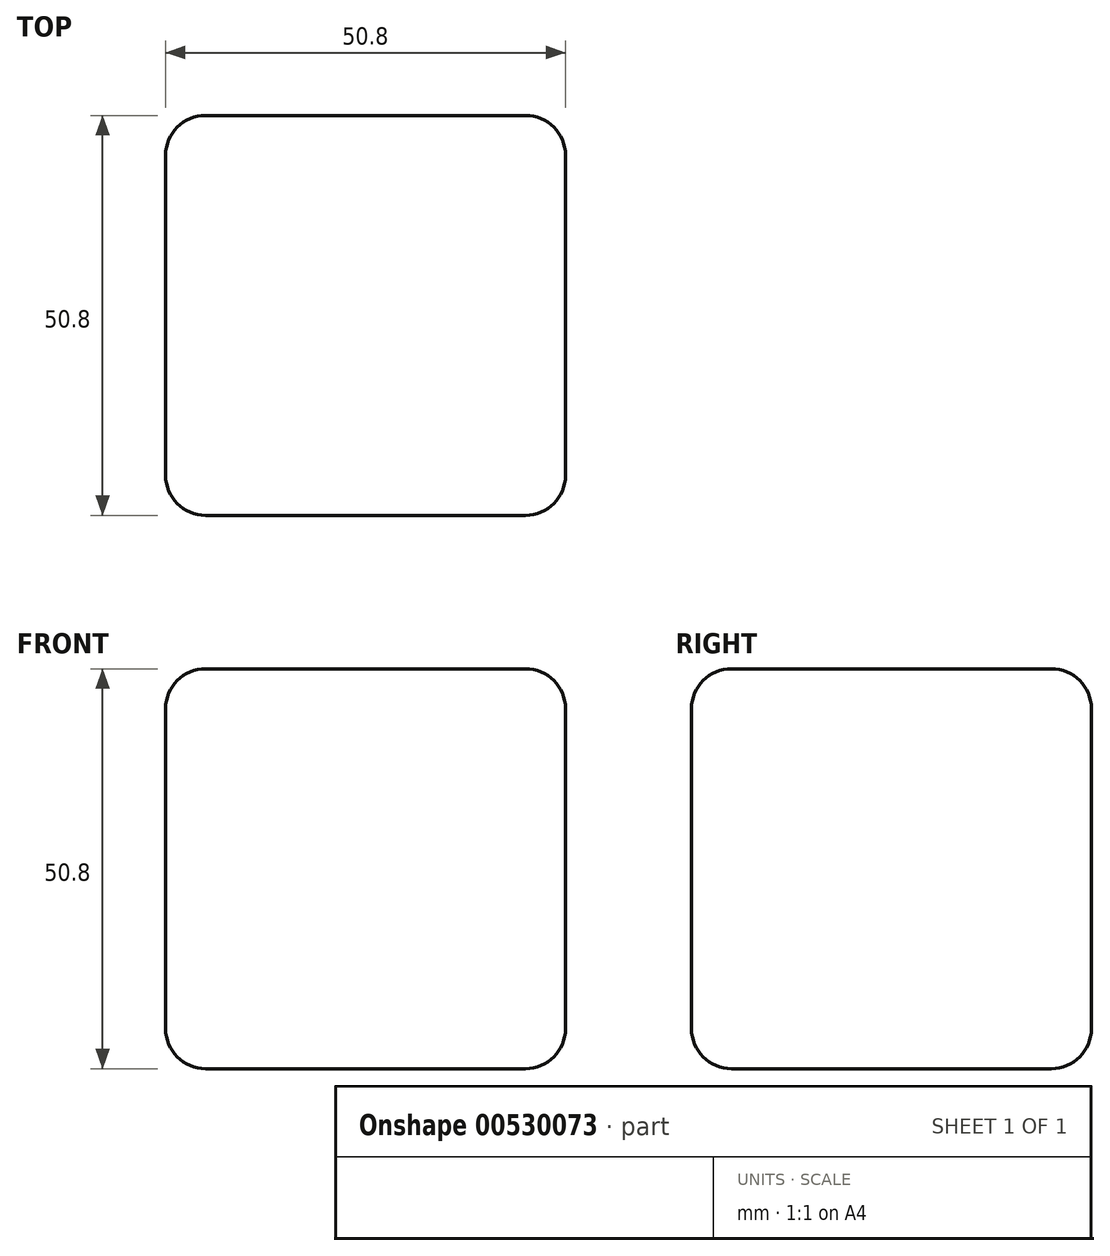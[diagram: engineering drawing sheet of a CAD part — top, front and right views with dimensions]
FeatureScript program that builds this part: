
annotation { "Feature Type Name" : "Feature", "Feature Type Description" : "" }
export const myFeature = defineFeature(function(context is Context, id is Id, definition is map)
    precondition{}
    {
        {
            var Q0;
            Q0=qCreatedBy(makeId("Front.planeOp"),FACE);
            var sketch = newSketch(context, id + "F0", { "sketchPlane" : qUnion([Q0])});
            skLineSegment(sketch, "E0.bottom", {"start": v(0, 0) * mm, "end": v(50.8, 0) * mm});
            skLineSegment(sketch, "E0.top", {"start": v(0, 50.8) * mm, "end": v(50.8, 50.8) * mm});
            skLineSegment(sketch, "E0.left", {"start": v(0, 0) * mm, "end": v(0, 50.8) * mm});
            skLineSegment(sketch, "E0.right", {"start": v(50.8, 0) * mm, "end": v(50.8, 50.8) * mm});
            skSolve(sketch);
        }
        {
            var Q0;
            Q0 = qSketchRegion(id + "F0", true);
            extrude(context, id + "F1", {"entities" : qUnion([Q0]), "endBound" : BoundingType.SYMMETRIC, "oppositeDirection" : true, "depth" : 50.8 * mm, "offsetDistance" : 25.4 * mm});
        }
        {
            var Q0;
            Q0=makeQuery(id+"F1.opExtrude","CAP_EDGE",EDGE,{"disambiguationData":[OSD([sQuery(id+"F0.wireOp",EDGE,"E0.top")])],"isStart":true});
            var Q1;
            Q1=makeQuery(id+"F1.opExtrude","SWEPT_EDGE",EDGE,{"disambiguationData":[OSD([sQuery(id+"F0.wireOp",EDGE,"E0.top"),sQuery(id+"F0.wireOp",EDGE,"E0.right")])]});
            var Q2;
            Q2=makeQuery(id+"F1.opExtrude","CAP_EDGE",EDGE,{"disambiguationData":[OSD([sQuery(id+"F0.wireOp",EDGE,"E0.right")])],"isStart":true});
            var Q3;
            Q3=makeQuery(id+"F1.opExtrude","CAP_EDGE",EDGE,{"disambiguationData":[OSD([sQuery(id+"F0.wireOp",EDGE,"E0.left")])],"isStart":true});
            var Q4;
            Q4=makeQuery(id+"F1.opExtrude","SWEPT_EDGE",EDGE,{"disambiguationData":[OSD([sQuery(id+"F0.wireOp",EDGE,"E0.top"),sQuery(id+"F0.wireOp",EDGE,"E0.left")])]});
            var Q5;
            Q5=makeQuery(id+"F1.opExtrude","CAP_EDGE",EDGE,{"disambiguationData":[OSD([sQuery(id+"F0.wireOp",EDGE,"E0.top")])],"isStart":false});
            var Q6;
            Q6=makeQuery(id+"F1.opExtrude","CAP_EDGE",EDGE,{"disambiguationData":[OSD([sQuery(id+"F0.wireOp",EDGE,"E0.left")])],"isStart":false});
            var Q7;
            Q7=makeQuery(id+"F1.opExtrude","CAP_EDGE",EDGE,{"disambiguationData":[OSD([sQuery(id+"F0.wireOp",EDGE,"E0.right")])],"isStart":false});
            var Q8;
            Q8=makeQuery(id+"F1.opExtrude","CAP_EDGE",EDGE,{"disambiguationData":[OSD([sQuery(id+"F0.wireOp",EDGE,"E0.bottom")])],"isStart":false});
            var Q9;
            Q9=makeQuery(id+"F1.opExtrude","SWEPT_EDGE",EDGE,{"disambiguationData":[OSD([sQuery(id+"F0.wireOp",EDGE,"E0.bottom"),sQuery(id+"F0.wireOp",EDGE,"E0.right")])]});
            var Q10;
            Q10=makeQuery(id+"F1.opExtrude","CAP_EDGE",EDGE,{"disambiguationData":[OSD([sQuery(id+"F0.wireOp",EDGE,"E0.bottom")])],"isStart":true});
            var Q11;
            Q11=makeQuery(id+"F1.opExtrude","SWEPT_EDGE",EDGE,{"disambiguationData":[OSD([sQuery(id+"F0.wireOp",EDGE,"E0.bottom"),sQuery(id+"F0.wireOp",EDGE,"E0.left")])]});
            fillet(context, id + "F2", {"entities" : qUnion([Q0, Q1, Q2, Q3, Q4, Q5, Q6, Q7, Q8, Q9, Q10, Q11]), "radius" : 5.08 * mm, "tangentPropagation" : true, "allowEdgeOverflow" : false});
        }
    });
